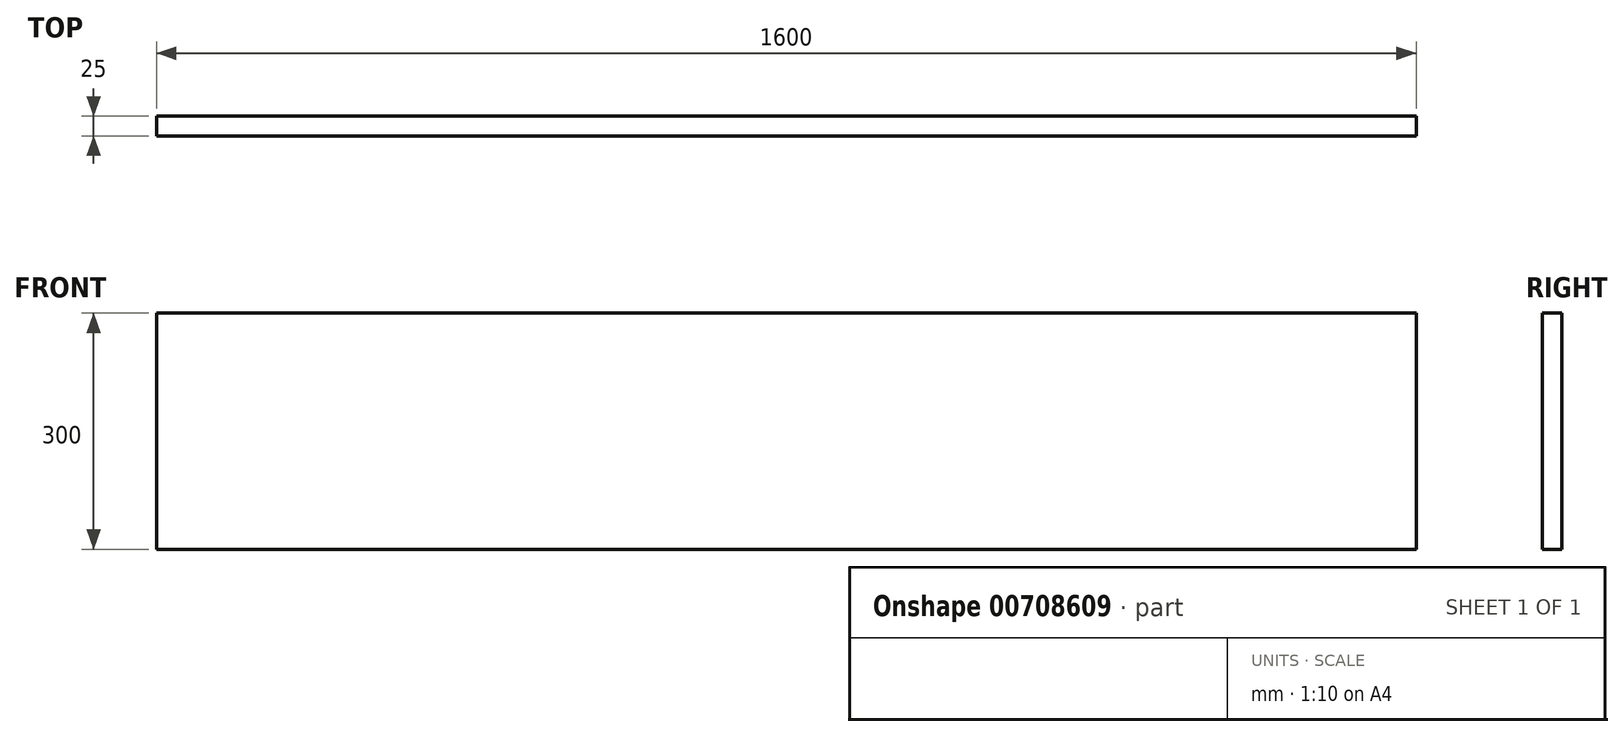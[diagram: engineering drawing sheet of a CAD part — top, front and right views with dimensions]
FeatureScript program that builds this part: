
annotation { "Feature Type Name" : "Feature", "Feature Type Description" : "" }
export const myFeature = defineFeature(function(context is Context, id is Id, definition is map)
    precondition{}
    {
        {
            var Q0;
            Q0=qCreatedBy(makeId("Front.planeOp"),FACE);
            var sketch = newSketch(context, id + "F0", { "sketchPlane" : qUnion([Q0])});
            skLineSegment(sketch, "E0.bottom", {"start": v(0, 0) * mm, "end": v(1600, 0) * mm});
            skLineSegment(sketch, "E0.top", {"start": v(0, 300) * mm, "end": v(1600, 300) * mm});
            skLineSegment(sketch, "E0.left", {"start": v(0, 0) * mm, "end": v(0, 300) * mm});
            skLineSegment(sketch, "E0.right", {"start": v(1600, 0) * mm, "end": v(1600, 300) * mm});
            skSolve(sketch);
        }
        {
            var Q0;
            Q0=makeQuery(id+"F0.imprint","IMPRINT",FACE,{"disambiguationData":[TD([[makeQuery(id+"F0.imprint","IMPRINT",EDGE,{"derivedFrom":sQuery(id+"F0.wireOp",EDGE,"E0.bottom")}),1.0]])]});
            extrude(context, id + "F1", {"entities" : qUnion([Q0]), "depth" : 25 * mm, "offsetDistance" : 25 * mm});
        }
    });
